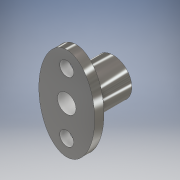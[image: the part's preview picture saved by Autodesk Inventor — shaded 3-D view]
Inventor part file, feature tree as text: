
AUTODESK INVENTOR PART (.ipt)
format: ipt  version: 2017 (Build 210142000, 142)  size: 128,512 bytes
history: native  units: mm
features: extrude x2, sketch x2
ambient origin geometry x8: Origin, YZ Plane, XZ Plane, XY Plane, X Axis, Y Axis, Z Axis, Center Point
bodies: Solid1 (feature_tree)
feature tree (4):
  extrude  "Extrusion1"  Depth=4.0mm
  extrude  "Extrusion2"  Depth=8.0mm
  sketch  "Sketch3"  dims[d0=6.0mm d2=4.0mm]
  sketch  "Sketch4"  dims[d3=10.0mm d5=3.0mm d9=6.502571mm d11=3.0mm d12=6.5mm d13=2.0mm d14=0.0mm d15=8.0mm d16=4.0mm d17=8.0mm d18=0.0mm]
